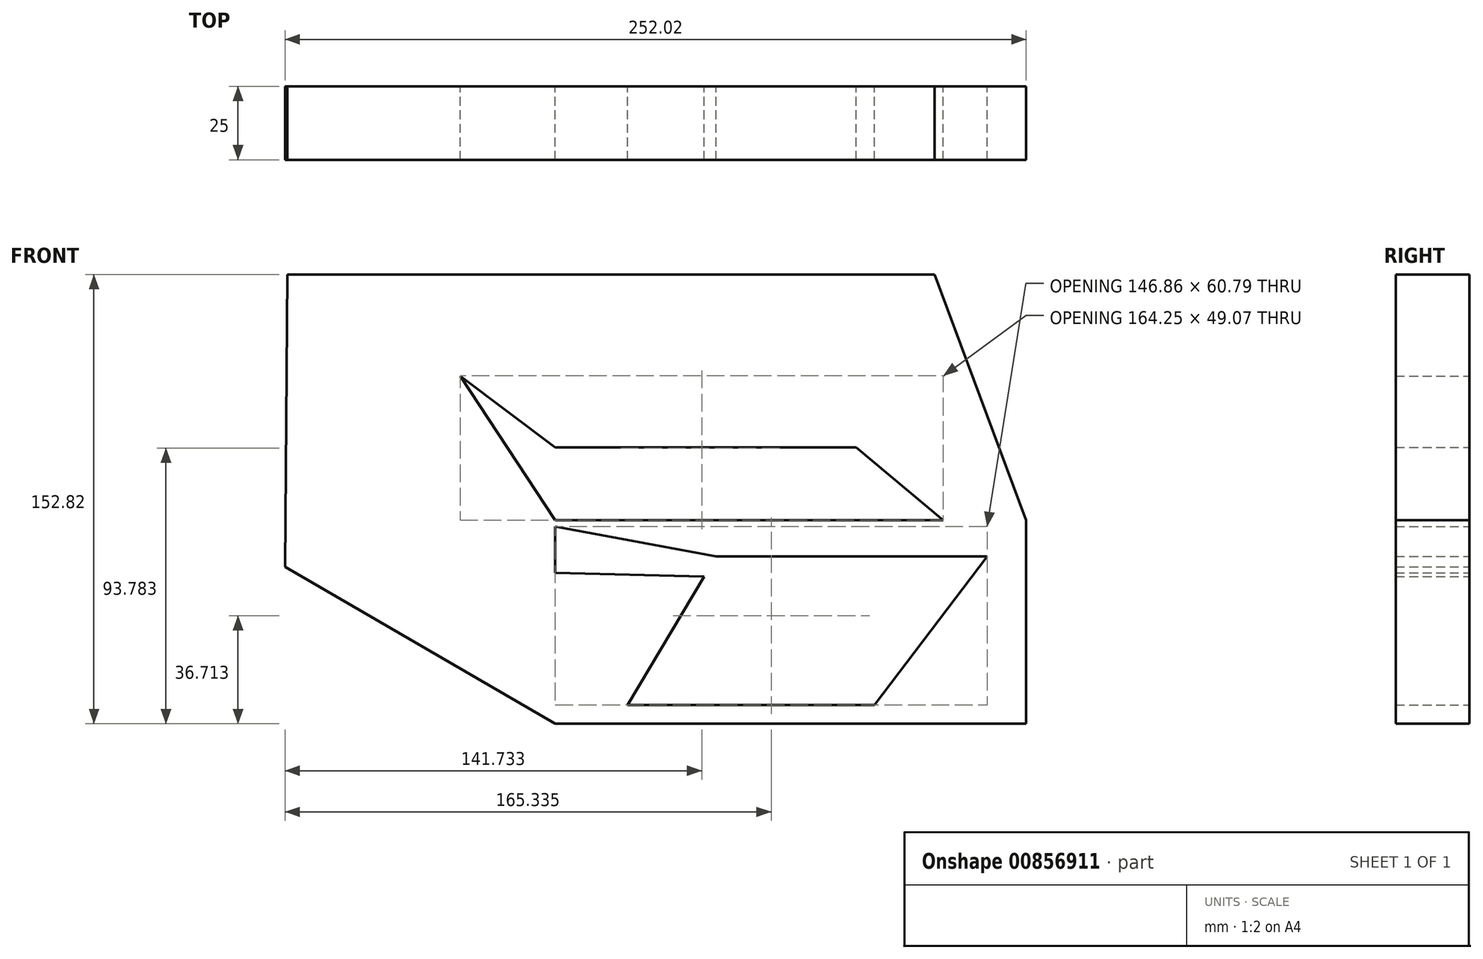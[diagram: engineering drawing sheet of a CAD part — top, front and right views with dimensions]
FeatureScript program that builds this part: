
annotation { "Feature Type Name" : "Feature", "Feature Type Description" : "" }
export const myFeature = defineFeature(function(context is Context, id is Id, definition is map)
    precondition{}
    {
        {
            var Q0;
            Q0=qCreatedBy(makeId("Front.planeOp"),FACE);
            var sketch = newSketch(context, id + "F0", { "sketchPlane" : qUnion([Q0])});
            skLineSegment(sketch, "E0", {"start": v(-35.28, 32.04) * mm, "end": v(56.95, 32.04) * mm});
            skLineSegment(sketch, "E1", {"start": v(56.95, 32.04) * mm, "end": v(18.61, -18.52) * mm});
            skLineSegment(sketch, "E2", {"start": v(18.61, -18.52) * mm, "end": v(-65.29, -18.52) * mm});
            skLineSegment(sketch, "E3", {"start": v(-65.29, -18.52) * mm, "end": v(-35.28, 32.04) * mm});
            skLineSegment(sketch, "E4", {"start": v(-9.17, -44.88) * mm, "end": v(-9.17, -86.86) * mm});
            skLineSegment(sketch, "E5.bottom", {"start": v(-89.9, -24.84) * mm, "end": v(70.21, -24.84) * mm});
            skLineSegment(sketch, "E5.top", {"start": v(-89.9, 44.4) * mm, "end": v(70.21, 44.4) * mm});
            skLineSegment(sketch, "E5.left", {"start": v(-89.9, -24.84) * mm, "end": v(-89.9, 44.4) * mm});
            skLineSegment(sketch, "E5.right", {"start": v(70.21, -24.84) * mm, "end": v(70.21, 44.4) * mm});
            skLineSegment(sketch, "E6", {"start": v(-89.9, 42.27) * mm, "end": v(-35.28, 32.04) * mm});
            skLineSegment(sketch, "E7", {"start": v(-65.29, -18.52) * mm, "end": v(-89.9, -24.84) * mm});
            skLineSegment(sketch, "E8", {"start": v(18.61, -18.52) * mm, "end": v(70.21, -24.84) * mm});
            skLineSegment(sketch, "E9", {"start": v(56.95, 32.04) * mm, "end": v(70.21, 44.4) * mm});
            skLineSegment(sketch, "E10", {"start": v(70.21, 44.4) * mm, "end": v(24.66, 93.48) * mm});
            skLineSegment(sketch, "E11", {"start": v(24.66, 93.48) * mm, "end": v(-122.2, 93.48) * mm});
            skLineSegment(sketch, "E12", {"start": v(-122.2, 93.48) * mm, "end": v(-89.9, 44.4) * mm});
            skLineSegment(sketch, "E13", {"start": v(54.97, 33.58) * mm, "end": v(12.46, 69.2) * mm});
            skLineSegment(sketch, "E14", {"start": v(12.46, 69.2) * mm, "end": v(-89.9, 69.2) * mm});
            skLineSegment(sketch, "E15", {"start": v(-89.9, 69.2) * mm, "end": v(-122.2, 93.48) * mm});
            skLineSegment(sketch, "E16", {"start": v(-89.9, 69.2) * mm, "end": v(-89.9, 44.4) * mm});
            skLineSegment(sketch, "E17", {"start": v(70.21, 44.4) * mm, "end": v(39.01, 127.98) * mm});
            skLineSegment(sketch, "E18", {"start": v(39.01, 127.98) * mm, "end": v(-181, 127.98) * mm});
            skLineSegment(sketch, "E19", {"start": v(-181, 127.98) * mm, "end": v(-89.9, 44.4) * mm});
            skLineSegment(sketch, "E20", {"start": v(-89.9, -24.84) * mm, "end": v(-181.81, 28.57) * mm});
            skLineSegment(sketch, "E21", {"start": v(-181.81, 28.57) * mm, "end": v(29.98, 23.68) * mm});
            skLineSegment(sketch, "E22", {"start": v(29.98, 23.68) * mm, "end": v(70.21, -24.84) * mm});
            skLineSegment(sketch, "E23", {"start": v(-181, 127.98) * mm, "end": v(-181.81, 28.57) * mm});
            skLineSegment(sketch, "E24", {"start": v(-89.9, 42.27) * mm, "end": v(-181.81, 28.57) * mm});
            skSolve(sketch);
        }
        {
            var Q0;
            Q0 = qSketchRegion(id + "F0", true);
            extrude(context, id + "F1", {"entities" : qUnion([Q0]), "depth" : 25 * mm, "offsetDistance" : 25 * mm});
        }
    });
